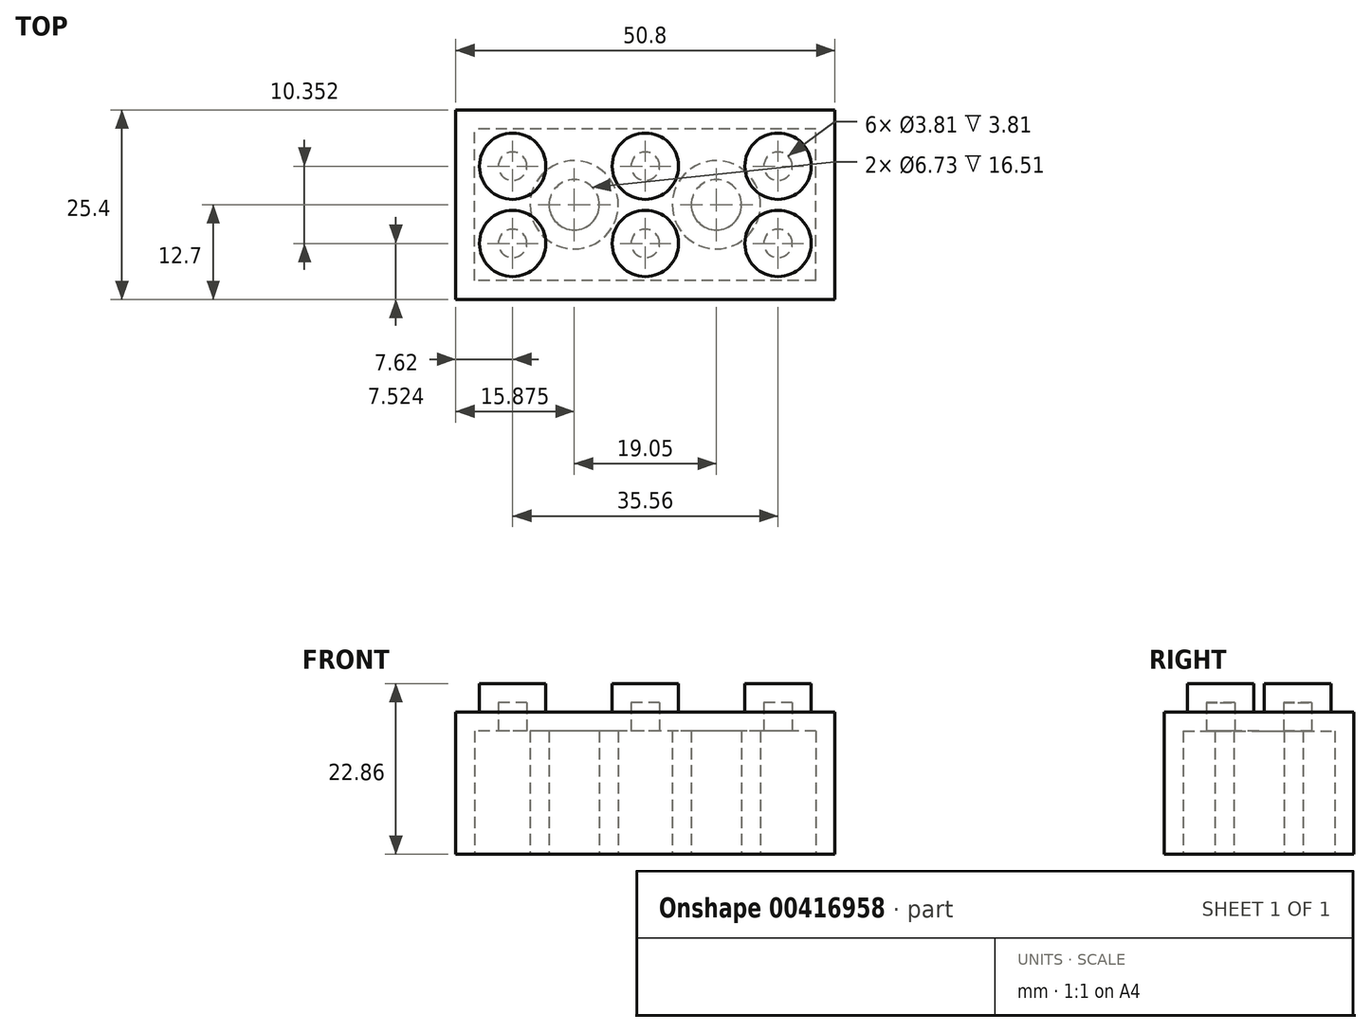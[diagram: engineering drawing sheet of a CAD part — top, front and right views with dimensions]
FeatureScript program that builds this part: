
annotation { "Feature Type Name" : "Feature", "Feature Type Description" : "" }
export const myFeature = defineFeature(function(context is Context, id is Id, definition is map)
    precondition{}
    {
        {
            var Q0;
            Q0=qCreatedBy(makeId("Top.planeOp"),FACE);
            var sketch = newSketch(context, id + "F0", { "sketchPlane" : qUnion([Q0])});
            skLineSegment(sketch, "E0.bottom", {"start": v(25.4, -12.7) * mm, "end": v(-25.4, -12.7) * mm});
            skLineSegment(sketch, "E0.top", {"start": v(25.4, 12.7) * mm, "end": v(-25.4, 12.7) * mm});
            skLineSegment(sketch, "E0.left", {"start": v(25.4, -12.7) * mm, "end": v(25.4, 12.7) * mm});
            skLineSegment(sketch, "E0.right", {"start": v(-25.4, -12.7) * mm, "end": v(-25.4, 12.7) * mm});
            skPoint(sketch, "E0.middle", {"position": v(0, 0) * mm});
            skSolve(sketch);
        }
        {
            var Q0;
            Q0=makeQuery(id+"F0.imprint","IMPRINT",FACE,{"disambiguationData":[TD([[makeQuery(id+"F0.imprint","IMPRINT",EDGE,{"derivedFrom":sQuery(id+"F0.wireOp",EDGE,"E0.bottom")}),-1.0]])]});
            extrude(context, id + "F1", {"entities" : qUnion([Q0]), "depth" : 19.05 * mm, "offsetDistance" : 25.4 * mm});
        }
        {
            var Q0;
            Q0=makeQuery(id+"F1.opExtrude","CAP_FACE",FACE,{"disambiguationData":[OSD([sQuery(id+"F0.wireOp",EDGE,"E0.bottom"),sQuery(id+"F0.wireOp",EDGE,"E0.top"),sQuery(id+"F0.wireOp",EDGE,"E0.left"),sQuery(id+"F0.wireOp",EDGE,"E0.right")])],"isStart":false});
            var sketch = newSketch(context, id + "F2", { "sketchPlane" : qUnion([Q0])});
            skCircle(sketch, "E1", {"center": v(-17.78, 5.18) * mm, "radius": 4.45 * mm});
            skCircle(sketch, "E2", {"center": v(0, 5.18) * mm, "radius": 4.45 * mm});
            skCircle(sketch, "E3", {"center": v(17.78, 5.18) * mm, "radius": 4.45 * mm});
            skCircle(sketch, "E4", {"center": v(0, -5.18) * mm, "radius": 4.45 * mm});
            skCircle(sketch, "E5", {"center": v(17.78, -5.18) * mm, "radius": 4.45 * mm});
            skCircle(sketch, "E6", {"center": v(-17.78, -5.18) * mm, "radius": 4.45 * mm});
            skLineSegment(sketch, "E7", {"start": v(-38.3, 5.18) * mm, "end": v(43.66, 5.18) * mm, "construction": true});
            skLineSegment(sketch, "E8", {"start": v(43.14, -5.18) * mm, "end": v(-40.91, -5.18) * mm, "construction": true});
            skLineSegment(sketch, "E9", {"start": v(-17.78, 5.18) * mm, "end": v(-17.78, -5.18) * mm, "construction": true});
            skLineSegment(sketch, "E10", {"start": v(0, 5.18) * mm, "end": v(0, -5.18) * mm, "construction": true});
            skLineSegment(sketch, "E11", {"start": v(17.78, 5.18) * mm, "end": v(17.78, -5.18) * mm, "construction": true});
            skCircle(sketch, "E12", {"center": v(-8.9, 0) * mm, "radius": 5.84 * mm, "construction": true});
            skPoint(sketch, "E12.first.point", {"position": v(-13.94, 2.94) * mm});
            skPoint(sketch, "E12.second.point", {"position": v(-3.84, 2.94) * mm});
            skPoint(sketch, "E12.third.point", {"position": v(-3.84, -2.94) * mm});
            skLineSegment(sketch, "E13.0", {"start": v(22.86, 10.16) * mm, "end": v(-22.86, 10.16) * mm, "construction": true});
            skLineSegment(sketch, "E13.1", {"start": v(22.86, -10.16) * mm, "end": v(22.86, 10.16) * mm, "construction": true});
            skLineSegment(sketch, "E13.2", {"start": v(22.86, -10.16) * mm, "end": v(-22.86, -10.16) * mm, "construction": true});
            skLineSegment(sketch, "E13.3", {"start": v(-22.86, -10.16) * mm, "end": v(-22.86, 10.16) * mm, "construction": true});
            skSolve(sketch);
        }
        {
            var Q0;
            Q0=makeQuery(id+"F2.imprint","IMPRINT",FACE,{"disambiguationData":[TD([[makeQuery(id+"F2.imprint","IMPRINT",EDGE,{"derivedFrom":sQuery(id+"F2.wireOp",EDGE,"E1")}),1.0]])]});
            var Q1;
            Q1=makeQuery(id+"F2.imprint","IMPRINT",FACE,{"disambiguationData":[TD([[makeQuery(id+"F2.imprint","IMPRINT",EDGE,{"derivedFrom":sQuery(id+"F2.wireOp",EDGE,"E2")}),1.0]])]});
            var Q2;
            Q2=makeQuery(id+"F2.imprint","IMPRINT",FACE,{"disambiguationData":[TD([[makeQuery(id+"F2.imprint","IMPRINT",EDGE,{"derivedFrom":sQuery(id+"F2.wireOp",EDGE,"E3")}),1.0]])]});
            var Q3;
            Q3=makeQuery(id+"F2.imprint","IMPRINT",FACE,{"disambiguationData":[TD([[makeQuery(id+"F2.imprint","IMPRINT",EDGE,{"derivedFrom":sQuery(id+"F2.wireOp",EDGE,"E5")}),1.0]])]});
            var Q4;
            Q4=makeQuery(id+"F2.imprint","IMPRINT",FACE,{"disambiguationData":[TD([[makeQuery(id+"F2.imprint","IMPRINT",EDGE,{"derivedFrom":sQuery(id+"F2.wireOp",EDGE,"E4")}),1.0]])]});
            var Q5;
            Q5=makeQuery(id+"F2.imprint","IMPRINT",FACE,{"disambiguationData":[TD([[makeQuery(id+"F2.imprint","IMPRINT",EDGE,{"derivedFrom":sQuery(id+"F2.wireOp",EDGE,"E6")}),1.0]])]});
            extrude(context, id + "F3", {"entities" : qUnion([Q0, Q1, Q2, Q3, Q4, Q5]), "operationType" : NewBodyOperationType.ADD, "depth" : 3.8 * mm, "offsetDistance" : 25.4 * mm});
        }
        {
            var Q0;
            Q0=makeQuery(id+"F1.opExtrude","CAP_FACE",FACE,{"disambiguationData":[OSD([sQuery(id+"F0.wireOp",EDGE,"E0.bottom"),sQuery(id+"F0.wireOp",EDGE,"E0.top"),sQuery(id+"F0.wireOp",EDGE,"E0.left"),sQuery(id+"F0.wireOp",EDGE,"E0.right")])],"isStart":true});
            shell(context, id + "F4", {"entities" : qUnion([Q0]), "thickness" : 2.54 * mm});
        }
        {
            var Q0;
            Q0=makeQuery(id+"F1.opExtrude","CAP_FACE",FACE,{"disambiguationData":[OSD([sQuery(id+"F0.wireOp",EDGE,"E0.bottom"),sQuery(id+"F0.wireOp",EDGE,"E0.top"),sQuery(id+"F0.wireOp",EDGE,"E0.left"),sQuery(id+"F0.wireOp",EDGE,"E0.right")])],"isStart":true});
            var sketch = newSketch(context, id + "F5", { "sketchPlane" : qUnion([Q0])});
            skCircle(sketch, "E14", {"center": v(-9.53, 0) * mm, "radius": 5.9 * mm});
            skCircle(sketch, "E15", {"center": v(9.53, 0) * mm, "radius": 5.9 * mm});
            skCircle(sketch, "E16.0", {"center": v(-9.53, 0) * mm, "radius": 3.37 * mm});
            skCircle(sketch, "E17.0", {"center": v(9.53, 0) * mm, "radius": 3.37 * mm});
            skSolve(sketch);
        }
        {
            var Q0;
            Q0=makeQuery(id+"F5.imprint","IMPRINT",FACE,{"disambiguationData":[TD([[makeQuery(id+"F5.imprint","IMPRINT",EDGE,{"derivedFrom":sQuery(id+"F5.wireOp",EDGE,"E14")}),1.0]])]});
            var Q1;
            Q1=makeQuery(id+"F5.imprint","IMPRINT",FACE,{"disambiguationData":[TD([[makeQuery(id+"F5.imprint","IMPRINT",EDGE,{"derivedFrom":sQuery(id+"F5.wireOp",EDGE,"E15")}),1.0]])]});
            var Q2;
            Q2=makeQuery(id+"F4.opShell","OFFSET_FACE",FACE,{"disambiguationData":[OSD([sQuery(id+"F0.wireOp",EDGE,"E0.bottom"),sQuery(id+"F0.wireOp",EDGE,"E0.top"),sQuery(id+"F0.wireOp",EDGE,"E0.left"),sQuery(id+"F0.wireOp",EDGE,"E0.right")])]});
            extrude(context, id + "F6", {"entities" : qUnion([Q0, Q1]), "operationType" : NewBodyOperationType.ADD, "endBound" : BoundingType.UP_TO_SURFACE, "oppositeDirection" : true, "endBoundEntityFace" : qUnion([Q2]), "depth" : 19.8 * mm, "offsetDistance" : 25.4 * mm});
        }
    });
